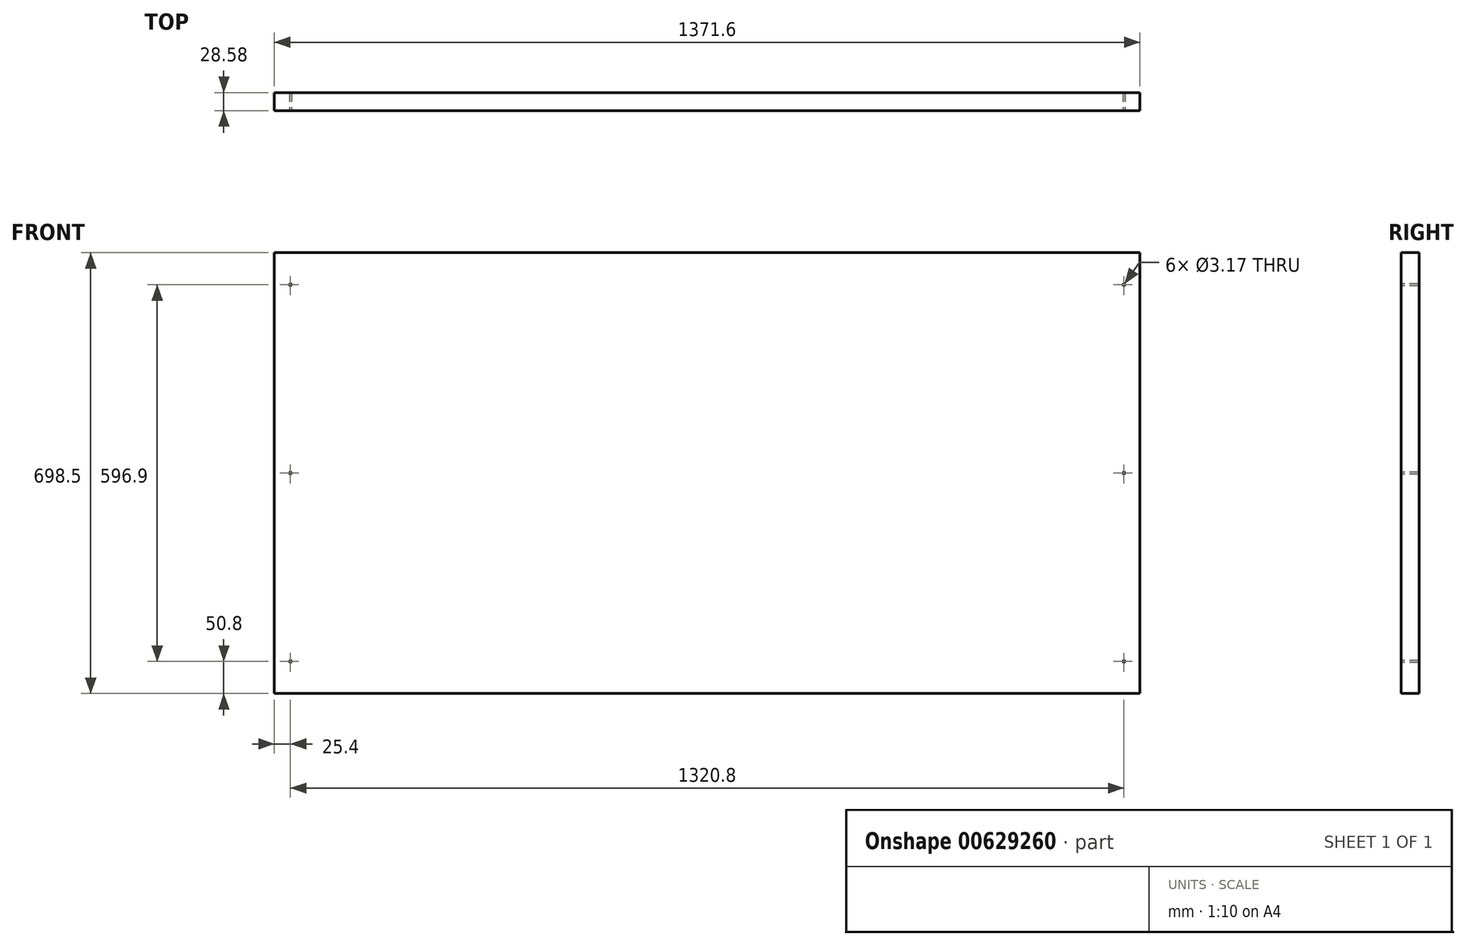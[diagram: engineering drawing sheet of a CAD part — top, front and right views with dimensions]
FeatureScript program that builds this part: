
annotation { "Feature Type Name" : "Feature", "Feature Type Description" : "" }
export const myFeature = defineFeature(function(context is Context, id is Id, definition is map)
    precondition{}
    {
        {
            var Q0;
            Q0=qCreatedBy(makeId("Front.planeOp"),FACE);
            var sketch = newSketch(context, id + "F0", { "sketchPlane" : qUnion([Q0])});
            skLineSegment(sketch, "E0.bottom", {"start": v(-685.8, 349.25) * mm, "end": v(685.8, 349.25) * mm});
            skLineSegment(sketch, "E0.top", {"start": v(-685.8, -349.25) * mm, "end": v(685.8, -349.25) * mm});
            skLineSegment(sketch, "E0.left", {"start": v(-685.8, 349.25) * mm, "end": v(-685.8, -349.25) * mm});
            skLineSegment(sketch, "E0.right", {"start": v(685.8, 349.25) * mm, "end": v(685.8, -349.25) * mm});
            skPoint(sketch, "E0.middle", {"position": v(0, 0) * mm});
            skSolve(sketch);
        }
        {
            var Q0;
            Q0=makeQuery(id+"F0.imprint","IMPRINT",FACE,{"disambiguationData":[TD([[makeQuery(id+"F0.imprint","IMPRINT",EDGE,{"derivedFrom":sQuery(id+"F0.wireOp",EDGE,"E0.bottom")}),-1.0]])]});
            extrude(context, id + "F1", {"entities" : qUnion([Q0]), "depth" : 28.57 * mm, "offsetDistance" : 25.4 * mm});
        }
        {
            var Q0;
            Q0=makeQuery(id+"F1.opExtrude","CAP_FACE",FACE,{"disambiguationData":[OSD([sQuery(id+"F0.wireOp",EDGE,"E0.bottom"),sQuery(id+"F0.wireOp",EDGE,"E0.top"),sQuery(id+"F0.wireOp",EDGE,"E0.left"),sQuery(id+"F0.wireOp",EDGE,"E0.right")])],"isStart":false});
            var sketch = newSketch(context, id + "F2", { "sketchPlane" : qUnion([Q0])});
            skLineSegment(sketch, "E1", {"start": v(-685.8, 349.25) * mm, "end": v(-660.4, 349.25) * mm});
            skLineSegment(sketch, "E2", {"start": v(-660.4, 349.25) * mm, "end": v(-660.4, 298.45) * mm});
            skLineSegment(sketch, "E3", {"start": v(-685.8, 0) * mm, "end": v(-660.4, 0) * mm});
            skLineSegment(sketch, "E4", {"start": v(-685.8, -349.25) * mm, "end": v(-660.4, -349.25) * mm});
            skLineSegment(sketch, "E5", {"start": v(-660.4, -349.25) * mm, "end": v(-660.4, -298.45) * mm});
            skLineSegment(sketch, "E6", {"start": v(685.8, 349.25) * mm, "end": v(660.4, 349.25) * mm});
            skLineSegment(sketch, "E7", {"start": v(660.4, 349.25) * mm, "end": v(660.4, 298.45) * mm});
            skLineSegment(sketch, "E8", {"start": v(685.8, -349.25) * mm, "end": v(660.4, -349.25) * mm});
            skLineSegment(sketch, "E9", {"start": v(660.4, -349.25) * mm, "end": v(660.4, -298.45) * mm});
            skLineSegment(sketch, "E10", {"start": v(685.8, 0) * mm, "end": v(660.4, 0) * mm});
            skPoint(sketch, "E10.endSnap0", {"position": v(685.8, 0) * mm});
            skPoint(sketch, "E11", {"position": v(-660.4, 298.45) * mm});
            skPoint(sketch, "E12", {"position": v(-660.4, 0) * mm});
            skPoint(sketch, "E13", {"position": v(-660.4, -298.45) * mm});
            skPoint(sketch, "E14", {"position": v(660.4, -298.45) * mm});
            skPoint(sketch, "E15", {"position": v(660.4, 0) * mm});
            skPoint(sketch, "E16", {"position": v(660.4, 298.45) * mm});
            skSolve(sketch);
        }
        {
            var Q0;
            Q0=sQuery(id+"F2.wireOp",VERTEX,"E11");
            var Q1;
            Q1=sQuery(id+"F2.wireOp",VERTEX,"E12");
            var Q2;
            Q2=sQuery(id+"F2.wireOp",VERTEX,"E13");
            var Q3;
            Q3=sQuery(id+"F2.wireOp",VERTEX,"E14");
            var Q4;
            Q4=sQuery(id+"F2.wireOp",VERTEX,"E15");
            var Q5;
            Q5=sQuery(id+"F2.wireOp",VERTEX,"E16");
            var Q6;
            Q6=makeQuery(id+"F1.opExtrude","SWEPT_BODY",BODY,{"disambiguationData":[OSD([sQuery(id+"F0.wireOp",EDGE,"E0.bottom"),sQuery(id+"F0.wireOp",EDGE,"E0.top"),sQuery(id+"F0.wireOp",EDGE,"E0.left"),sQuery(id+"F0.wireOp",EDGE,"E0.right")])]});
            hole(context, id + "F3", {"style" : HoleStyle.SIMPLE, "endStyle" : HoleEndStyle.BLIND, "holeDiameter" : 3.17 * mm, "majorDiameter" : 6.35 * mm, "holeDepth" : 31.75 * mm, "isTappedThrough" : true, "tappedDepth" : 12.7 * mm, "tapClearance" : 3, "startFromSketch" : true, "locations" : qUnion([Q0, Q1, Q2, Q3, Q4, Q5]), "scope" : qUnion([Q6])});
        }
    });
